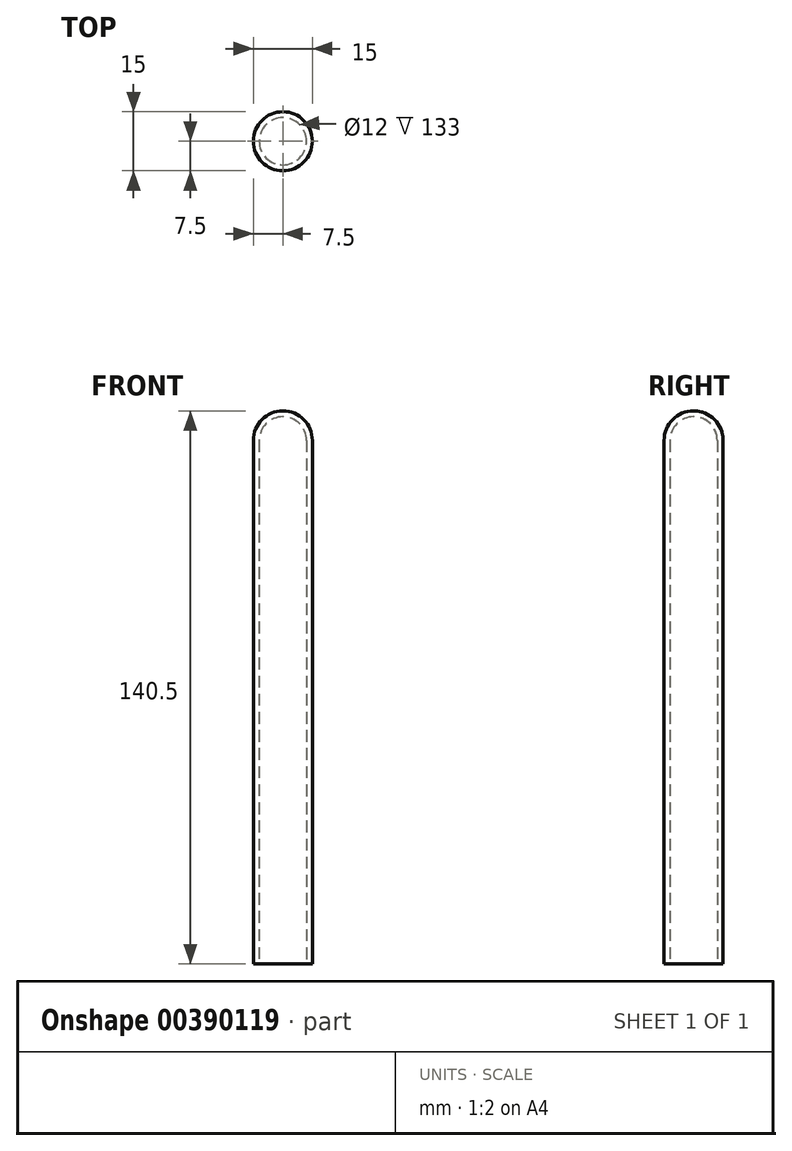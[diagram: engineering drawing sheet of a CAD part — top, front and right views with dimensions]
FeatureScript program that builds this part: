
annotation { "Feature Type Name" : "Feature", "Feature Type Description" : "" }
export const myFeature = defineFeature(function(context is Context, id is Id, definition is map)
    precondition{}
    {
        {
            var Q0;
            Q0=qCreatedBy(makeId("Top.planeOp"),FACE);
            var sketch = newSketch(context, id + "F0", { "sketchPlane" : qUnion([Q0])});
            skCircle(sketch, "E0", {"center": v(0, 0) * mm, "radius": 6 * mm});
            skCircle(sketch, "E1", {"center": v(0, 0) * mm, "radius": 7.5 * mm});
            skSolve(sketch);
        }
        {
            var Q0;
            Q0 = qSketchRegion(id + "F0", true);
            extrude(context, id + "F1", {"entities" : qUnion([Q0]), "depth" : 133 * mm});
        }
        {
            var Q0;
            Q0=qCreatedBy(makeId("Right.planeOp"),FACE);
            var sketch = newSketch(context, id + "F2", { "sketchPlane" : qUnion([Q0])});
            skLineSegment(sketch, "E2.0", {"start": v(-7.5, 133) * mm, "end": v(-7, 133) * mm});
            skArc(sketch, "E3", {"start": v(0, 140.5) * mm, "mid": v(-5.3, 138.3) * mm, "end": v(-7.5, 133) * mm});
            skLineSegment(sketch, "E4", {"start": v(0, 140) * mm, "end": v(0, 140.5) * mm});
            skArc(sketch, "E5", {"start": v(0, 139) * mm, "mid": v(-4.24, 137.24) * mm, "end": v(-6, 133) * mm});
            skLineSegment(sketch, "E6", {"start": v(0, 140) * mm, "end": v(0, 139) * mm});
            skLineSegment(sketch, "E7", {"start": v(-7, 133) * mm, "end": v(-6, 133) * mm});
            skSolve(sketch);
        }
        {
            var Q0;
            Q0 = qSketchRegion(id + "F2", true);
            var Q1;
            Q1=makeQuery(id+"F1.opExtrude","SWEPT_FACE",FACE,{"disambiguationData":[OSD([sQuery(id+"F0.wireOp",EDGE,"E1")])]});
            revolve(context, id + "F3", {"operationType" : NewBodyOperationType.ADD, "entities" : qUnion([Q0]), "axis" : qUnion([Q1]), "revolveType" : RevolveType.FULL});
        }
    });
